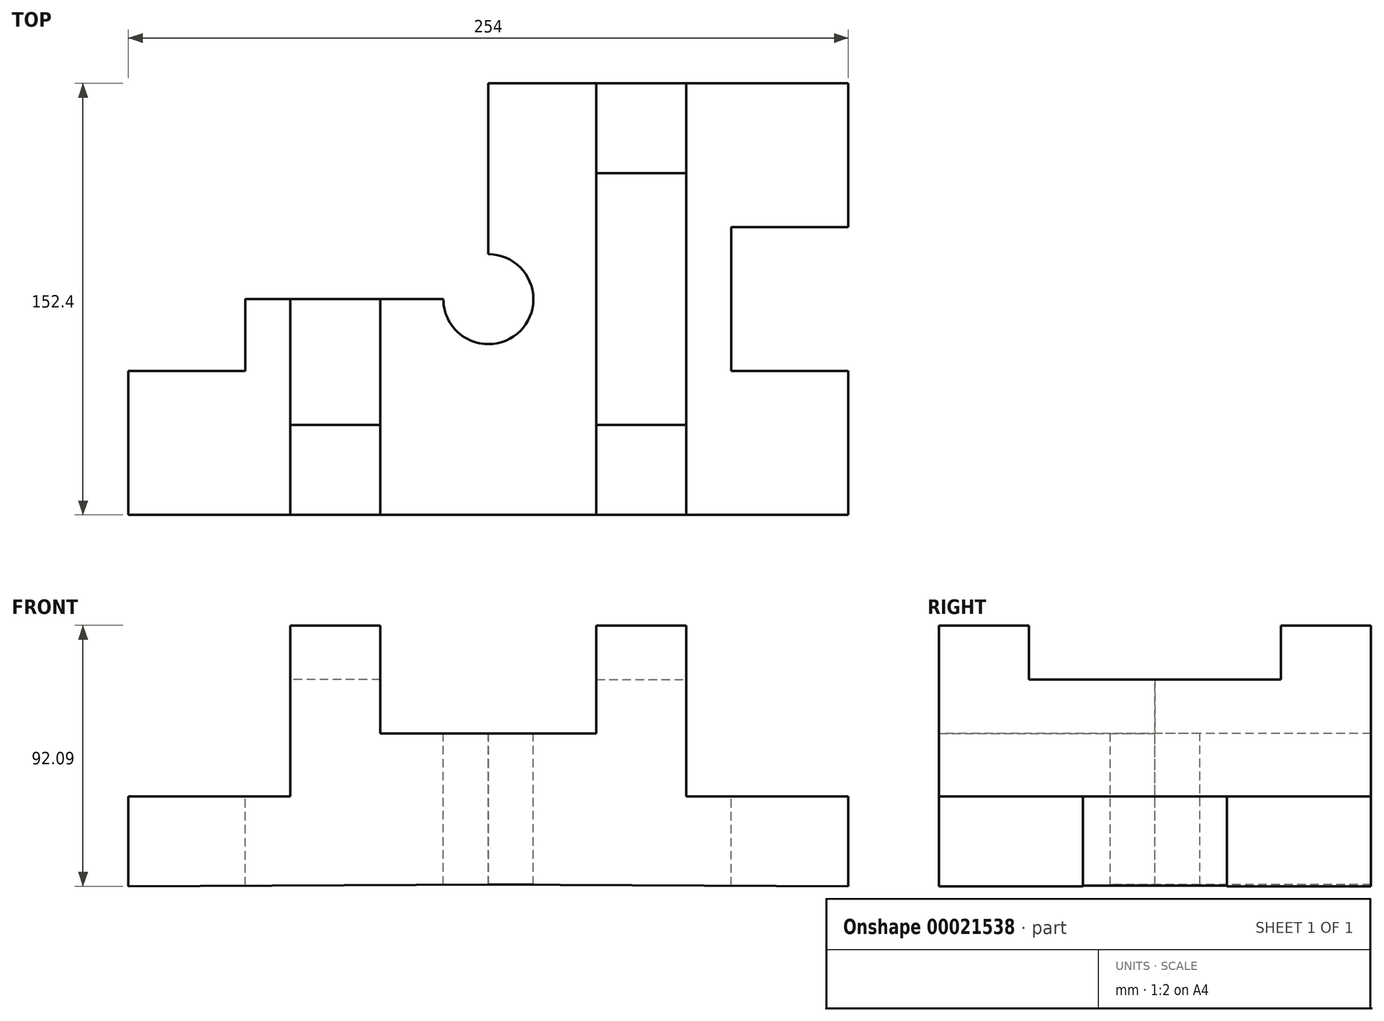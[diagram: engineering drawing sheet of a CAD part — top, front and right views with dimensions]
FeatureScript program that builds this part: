
annotation { "Feature Type Name" : "Feature", "Feature Type Description" : "" }
export const myFeature = defineFeature(function(context is Context, id is Id, definition is map)
    precondition{}
    {
        {
            var Q0;
            Q0=qCreatedBy(makeId("Front.planeOp"),FACE);
            var sketch = newSketch(context, id + "F0", { "sketchPlane" : qUnion([Q0])});
            skLineSegment(sketch, "E0", {"start": v(-65.95, -30.08) * mm, "end": v(61.05, -30.7) * mm});
            skLineSegment(sketch, "E1", {"start": v(61.05, -30.7) * mm, "end": v(61.05, 1.04) * mm});
            skLineSegment(sketch, "E2", {"start": v(61.05, 1.04) * mm, "end": v(3.9, 1.04) * mm});
            skLineSegment(sketch, "E3", {"start": v(3.9, 1.04) * mm, "end": v(3.9, 61.37) * mm});
            skLineSegment(sketch, "E4", {"start": v(3.9, 61.37) * mm, "end": v(-27.85, 61.37) * mm});
            skLineSegment(sketch, "E5", {"start": v(-27.85, 61.37) * mm, "end": v(-27.85, 23.27) * mm});
            skLineSegment(sketch, "E6", {"start": v(-27.85, 23.27) * mm, "end": v(-65.95, 23.27) * mm});
            skLineSegment(sketch, "E7", {"start": v(-65.95, 23.27) * mm, "end": v(-65.95, -30.08) * mm});
            skSolve(sketch);
        }
        {
            var Q0;
            Q0 = qSketchRegion(id + "F0", true);
            var Q1;
            Q1 = qSketchRegion(id + "F4", true);
            extrude(context, id + "F1", {"entities" : qUnion([Q0, Q1]), "depth" : 76.2 * mm});
        }
        {
            var Q0;
            Q0=makeQuery(id+"F1.opExtrude","SWEPT_FACE",FACE,{"disambiguationData":[OSD([sQuery(id+"F0.wireOp",EDGE,"E2")])]});
            var sketch = newSketch(context, id + "F2", { "sketchPlane" : qUnion([Q0])});
            skLineSegment(sketch, "E8", {"start": v(19.77, -25.4) * mm, "end": v(61.05, -25.4) * mm});
            skLineSegment(sketch, "E9", {"start": v(19.77, -25.4) * mm, "end": v(19.77, 0) * mm});
            skSolve(sketch);
        }
        {
            var Q0;
            Q0 = qSketchRegion(id + "F2", true);
            var Q1;
            {var subQ2=sQuery(id+"F2.wireOp",EDGE,"E8");Q1=makeQuery(id+"F2.imprint","IMPRINT",FACE,{"disambiguationData":[TD([[makeQuery(id+"F2.imprint","IMPRINT",EDGE,{"derivedFrom":subQ2}),1.0]])]});}
            extrude(context, id + "F3", {"entities" : qUnion([Q0, Q1]), "operationType" : NewBodyOperationType.REMOVE, "oppositeDirection" : true, "depth" : 76.2 * mm});
        }
        {
            var Q0;
            Q0=makeQuery(id+"F1.opExtrude","SWEPT_FACE",FACE,{"disambiguationData":[OSD([sQuery(id+"F0.wireOp",EDGE,"E3")])]});
            var sketch = newSketch(context, id + "F4", { "sketchPlane" : qUnion([Q0])});
            skLineSegment(sketch, "E10", {"start": v(-76.2, 61.37) * mm, "end": v(-44.45, 61.37) * mm});
            skLineSegment(sketch, "E11", {"start": v(-44.45, 61.37) * mm, "end": v(-44.45, 42.32) * mm});
            skLineSegment(sketch, "E12", {"start": v(-44.45, 42.32) * mm, "end": v(0, 42.32) * mm});
            skSolve(sketch);
        }
        {
            var Q0;
            {var subQ5=sQuery(id+"F4.wireOp",EDGE,"E11");Q0=makeQuery(id+"F4.imprint","IMPRINT",FACE,{"disambiguationData":[TD([[makeQuery(id+"F4.imprint","IMPRINT",EDGE,{"derivedFrom":subQ5}),1.0]])]});}
            extrude(context, id + "F5", {"entities" : qUnion([Q0]), "operationType" : NewBodyOperationType.REMOVE, "oppositeDirection" : true, "depth" : 76.2 * mm});
        }
        {
            var Q0;
            Q0=makeQuery(id+"F1.opExtrude","SWEPT_FACE",FACE,{"disambiguationData":[OSD([sQuery(id+"F0.wireOp",EDGE,"E6")])]});
            var sketch = newSketch(context, id + "F6", { "sketchPlane" : qUnion([Q0])});
            skCircle(sketch, "E13", {"center": v(-65.95, 0) * mm, "radius": 15.88 * mm});
            skSolve(sketch);
        }
        {
            var Q0;
            {var subQ0=sQuery(id+"F0.wireOp",EDGE,"E6");var subQ1=makeQuery(id+"F1.opExtrude","CAP_EDGE",EDGE,{"disambiguationData":[OSD([subQ0])],"isStart":true});var subQ2=sQuery(id+"F6.wireOp",EDGE,"E13");var subQ3=makeQuery(id+"F6.imprint","INTERSECT",VERTEX,{"derivedFrom":[subQ1,subQ2]});Q0=makeQuery(id+"F6.imprint","IMPRINT",FACE,{"disambiguationData":[TD([[makeQuery(id+"F6.imprint","IMPRINT",EDGE,{"disambiguationData":[TD([[subQ3,1.0]])],"derivedFrom":subQ2}),1.0]])]});}
            extrude(context, id + "F7", {"entities" : qUnion([Q0]), "operationType" : NewBodyOperationType.REMOVE, "oppositeDirection" : true, "depth" : 76.2 * mm});
        }
        {
            var Q0;
            Q0=makeQuery(id+"F1.opExtrude","SWEPT_BODY",BODY,{"disambiguationData":[OSD([sQuery(id+"F0.wireOp",EDGE,"E0"),sQuery(id+"F0.wireOp",EDGE,"E1"),sQuery(id+"F0.wireOp",EDGE,"E2"),sQuery(id+"F0.wireOp",EDGE,"E3"),sQuery(id+"F0.wireOp",EDGE,"E4"),sQuery(id+"F0.wireOp",EDGE,"E5"),sQuery(id+"F0.wireOp",EDGE,"E6"),sQuery(id+"F0.wireOp",EDGE,"E7")])]});
            var Q1;
            Q1=makeQuery(id+"F1.opExtrude","CAP_FACE",FACE,{"disambiguationData":[OSD([sQuery(id+"F0.wireOp",EDGE,"E0"),sQuery(id+"F0.wireOp",EDGE,"E1"),sQuery(id+"F0.wireOp",EDGE,"E2"),sQuery(id+"F0.wireOp",EDGE,"E3"),sQuery(id+"F0.wireOp",EDGE,"E4"),sQuery(id+"F0.wireOp",EDGE,"E5"),sQuery(id+"F0.wireOp",EDGE,"E6"),sQuery(id+"F0.wireOp",EDGE,"E7")])],"isStart":true});
            var Q2;
            Q2=makeQuery(id+"F1.opExtrude","CAP_FACE",FACE,{"disambiguationData":[OSD([sQuery(id+"F0.wireOp",EDGE,"E0"),sQuery(id+"F0.wireOp",EDGE,"E1"),sQuery(id+"F0.wireOp",EDGE,"E2"),sQuery(id+"F0.wireOp",EDGE,"E3"),sQuery(id+"F0.wireOp",EDGE,"E4"),sQuery(id+"F0.wireOp",EDGE,"E5"),sQuery(id+"F0.wireOp",EDGE,"E6"),sQuery(id+"F0.wireOp",EDGE,"E7")])],"isStart":true});
            mirror(context, id + "F8", {"entities" : qUnion([Q0]), "faces" : qUnion([Q1]), "mirrorPlane" : qUnion([Q2])});
        }
        {
            var Q0;
            Q0=makeQuery(id+"F1.opExtrude","SWEPT_BODY",BODY,{"disambiguationData":[OSD([sQuery(id+"F0.wireOp",EDGE,"E0"),sQuery(id+"F0.wireOp",EDGE,"E1"),sQuery(id+"F0.wireOp",EDGE,"E2"),sQuery(id+"F0.wireOp",EDGE,"E3"),sQuery(id+"F0.wireOp",EDGE,"E4"),sQuery(id+"F0.wireOp",EDGE,"E5"),sQuery(id+"F0.wireOp",EDGE,"E6"),sQuery(id+"F0.wireOp",EDGE,"E7")])]});
            var Q1;
            Q1=makeQuery(id+"F8.opPattern","COPY",FACE,{"derivedFrom":makeQuery(id+"F1.opExtrude","SWEPT_FACE",FACE,{"disambiguationData":[OSD([sQuery(id+"F0.wireOp",EDGE,"E7")])]}),"instanceName":"1"});
            mirror(context, id + "F9", {"operationType" : NewBodyOperationType.ADD, "entities" : qUnion([Q0]), "mirrorPlane" : qUnion([Q1])});
        }
    });
